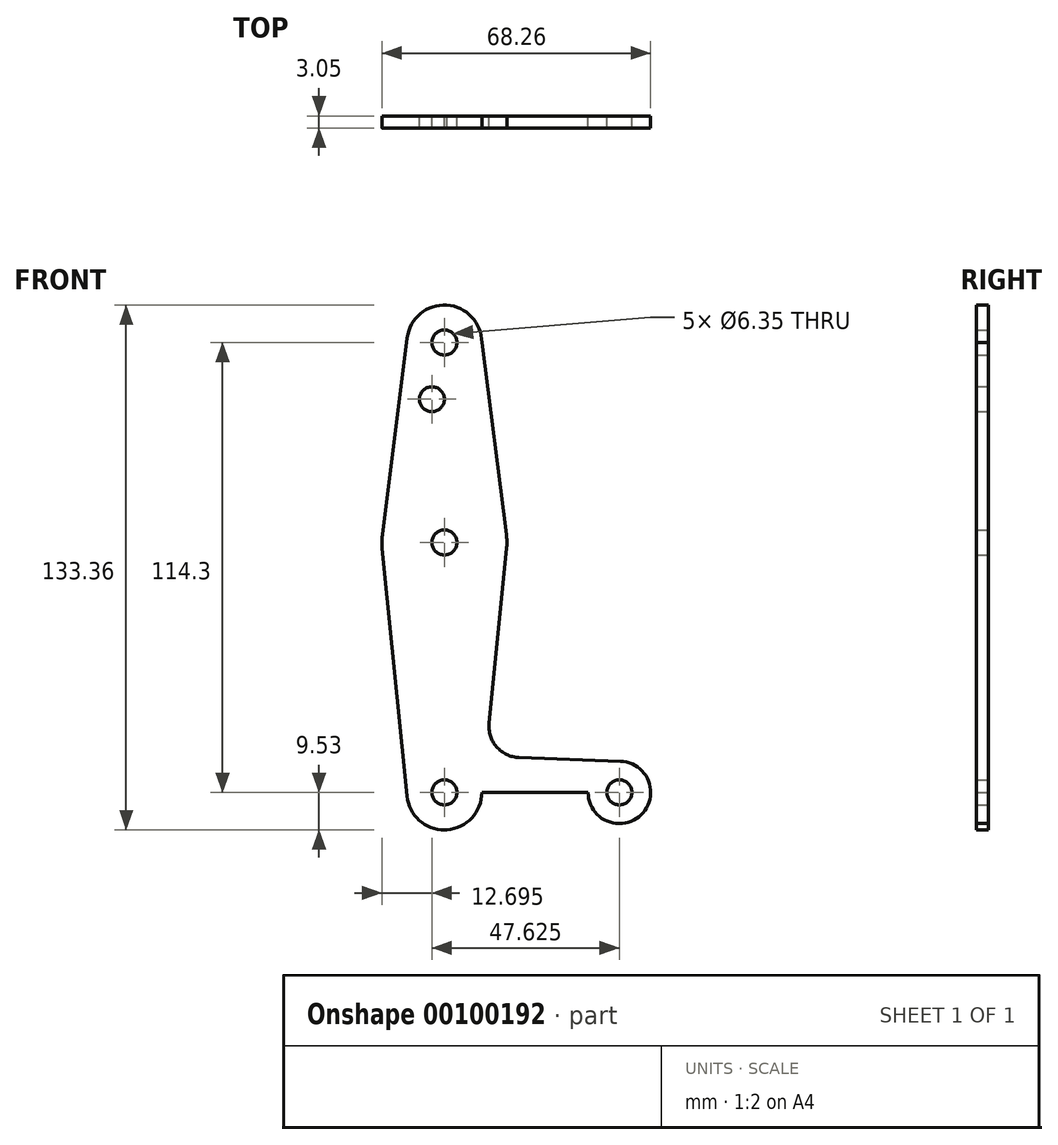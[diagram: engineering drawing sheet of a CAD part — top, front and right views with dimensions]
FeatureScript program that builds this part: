
annotation { "Feature Type Name" : "Feature", "Feature Type Description" : "" }
export const myFeature = defineFeature(function(context is Context, id is Id, definition is map)
    precondition{}
    {
        {
            var Q0;
            Q0=qCreatedBy(makeId("Front.planeOp"),FACE);
            var sketch = newSketch(context, id + "F0", { "sketchPlane" : qUnion([Q0])});
            skCircle(sketch, "E0", {"center": v(0, 0) * mm, "radius": 9.53 * mm});
            skLineSegment(sketch, "E1", {"start": v(0, 0) * mm, "end": v(0, 114.3) * mm});
            skCircle(sketch, "E2", {"center": v(0, 114.3) * mm, "radius": 9.53 * mm});
            skCircle(sketch, "E3", {"center": v(0, 63.5) * mm, "radius": 15.88 * mm});
            skCircle(sketch, "E4", {"center": v(44.45, 0) * mm, "radius": 7.94 * mm});
            skLineSegment(sketch, "E5", {"start": v(0, 0) * mm, "end": v(44.45, 0) * mm});
            skLineSegment(sketch, "E6", {"start": v(-9.45, 115.5) * mm, "end": v(-15.75, 65.48) * mm});
            skLineSegment(sketch, "E7", {"start": v(9.52, 114.3) * mm, "end": v(15.75, 65.5) * mm});
            skLineSegment(sketch, "E8", {"start": v(-15.8, 61.91) * mm, "end": v(-9.48, -0.95) * mm});
            skLineSegment(sketch, "E9", {"start": v(15.8, 61.91) * mm, "end": v(11.34, 17.6) * mm});
            skLineSegment(sketch, "E10", {"start": v(0, -9.52) * mm, "end": v(44.73, -7.93) * mm});
            skLineSegment(sketch, "E11", {"start": v(18.97, 8.85) * mm, "end": v(44.73, 7.93) * mm});
            skArc(sketch, "E12.filletArc", {"start": v(11.34, 17.6) * mm, "mid": v(13.26, 11.57) * mm, "end": v(18.97, 8.85) * mm});
            skCircle(sketch, "E13", {"center": v(0, 114.3) * mm, "radius": 3.18 * mm});
            skCircle(sketch, "E14", {"center": v(0, 63.5) * mm, "radius": 3.18 * mm});
            skCircle(sketch, "E15", {"center": v(0, 0) * mm, "radius": 3.18 * mm});
            skCircle(sketch, "E16", {"center": v(44.45, 0) * mm, "radius": 3.18 * mm});
            skCircle(sketch, "E17", {"center": v(-3.18, 99.89) * mm, "radius": 3.18 * mm});
            skSolve(sketch);
        }
        {
            var Q0;
            Q0=makeQuery(id+"F0.imprint","IMPRINT",FACE,{"disambiguationData":[TD([[makeQuery(id+"F0.imprint","IMPRINT",EDGE,{"derivedFrom":sQuery(id+"F0.wireOp",EDGE,"E13")}),-1.0]])]});
            var Q1;
            {var subQ0=sQuery(id+"F0.wireOp",EDGE,"E6");Q1=makeQuery(id+"F0.imprint","IMPRINT",FACE,{"disambiguationData":[TD([[makeQuery(id+"F0.imprint","IMPRINT",EDGE,{"derivedFrom":subQ0}),1.0]])]});}
            var Q2;
            {var subQ0=sQuery(id+"F0.wireOp",EDGE,"E7");Q2=makeQuery(id+"F0.imprint","IMPRINT",FACE,{"disambiguationData":[TD([[makeQuery(id+"F0.imprint","IMPRINT",EDGE,{"derivedFrom":subQ0}),-1.0]])]});}
            var Q3;
            {var subQ0=sQuery(id+"F0.wireOp",EDGE,"E3");var subQ3=sQuery(id+"F0.wireOp",EDGE,"E1");var subQ8=makeQuery(id+"F0.imprint","INTERSECT",VERTEX,{"disambiguationData":[OD(0.0)],"derivedFrom":[subQ3,subQ0]});Q3=makeQuery(id+"F0.imprint","IMPRINT",FACE,{"disambiguationData":[TD([[makeQuery(id+"F0.imprint","IMPRINT",EDGE,{"disambiguationData":[TD([[subQ8,-1.0]])],"derivedFrom":subQ3}),1.0]])]});}
            var Q4;
            {var subQ0=sQuery(id+"F0.wireOp",EDGE,"E3");var subQ2=sQuery(id+"F0.wireOp",EDGE,"E1");var subQ3=makeQuery(id+"F0.imprint","INTERSECT",VERTEX,{"disambiguationData":[OD(0.0)],"derivedFrom":[subQ2,subQ0]});Q4=makeQuery(id+"F0.imprint","IMPRINT",FACE,{"disambiguationData":[TD([[makeQuery(id+"F0.imprint","IMPRINT",EDGE,{"disambiguationData":[TD([[subQ3,-1.0]])],"derivedFrom":subQ2}),-1.0]])]});}
            var Q5;
            {var subQ0=sQuery(id+"F0.wireOp",EDGE,"E8");Q5=makeQuery(id+"F0.imprint","IMPRINT",FACE,{"disambiguationData":[TD([[makeQuery(id+"F0.imprint","IMPRINT",EDGE,{"derivedFrom":subQ0}),1.0]])]});}
            var Q6;
            {var subQ4=sQuery(id+"F0.wireOp",EDGE,"E9");Q6=makeQuery(id+"F0.imprint","IMPRINT",FACE,{"disambiguationData":[TD([[makeQuery(id+"F0.imprint","IMPRINT",EDGE,{"derivedFrom":subQ4}),-1.0]])]});}
            var Q7;
            {var subQ1=sQuery(id+"F0.wireOp",EDGE,"E0");var subQ9=makeQuery(id+"F0.imprint","INTERSECT",VERTEX,{"derivedFrom":[subQ1,sQuery(id+"F0.wireOp",EDGE,"E8")]});Q7=makeQuery(id+"F0.imprint","IMPRINT",FACE,{"disambiguationData":[TD([[makeQuery(id+"F0.imprint","IMPRINT",EDGE,{"disambiguationData":[TD([[subQ9,1.0]])],"derivedFrom":subQ1}),1.0]])]});}
            var Q8;
            {var subQ0=sQuery(id+"F0.wireOp",EDGE,"E1");var subQ1=sQuery(id+"F0.wireOp",EDGE,"E0");var subQ2=makeQuery(id+"F0.imprint","INTERSECT",VERTEX,{"derivedFrom":[subQ1,subQ0]});Q8=makeQuery(id+"F0.imprint","IMPRINT",FACE,{"disambiguationData":[TD([[makeQuery(id+"F0.imprint","IMPRINT",EDGE,{"disambiguationData":[TD([[subQ2,1.0]])],"derivedFrom":subQ1}),1.0]])]});}
            var Q9;
            {var subQ0=sQuery(id+"F0.wireOp",EDGE,"E10");var subQ1=sQuery(id+"F0.wireOp",EDGE,"E0");var subQ2=makeQuery(id+"F0.imprint","INTERSECT",VERTEX,{"disambiguationData":[OD(1.0)],"derivedFrom":[subQ1,subQ0]});Q9=makeQuery(id+"F0.imprint","IMPRINT",FACE,{"disambiguationData":[TD([[makeQuery(id+"F0.imprint","IMPRINT",EDGE,{"disambiguationData":[TD([[subQ2,-1.0]])],"derivedFrom":subQ1}),-1.0]])]});}
            var Q10;
            Q10=makeQuery(id+"F0.imprint","IMPRINT",FACE,{"disambiguationData":[TD([[makeQuery(id+"F0.imprint","IMPRINT",EDGE,{"derivedFrom":sQuery(id+"F0.wireOp",EDGE,"E16")}),-1.0]])]});
            extrude(context, id + "F1", {"entities" : qUnion([Q0, Q1, Q2, Q3, Q4, Q5, Q6, Q7, Q8, Q9, Q10]), "depth" : 3.05 * mm});
        }
    });
